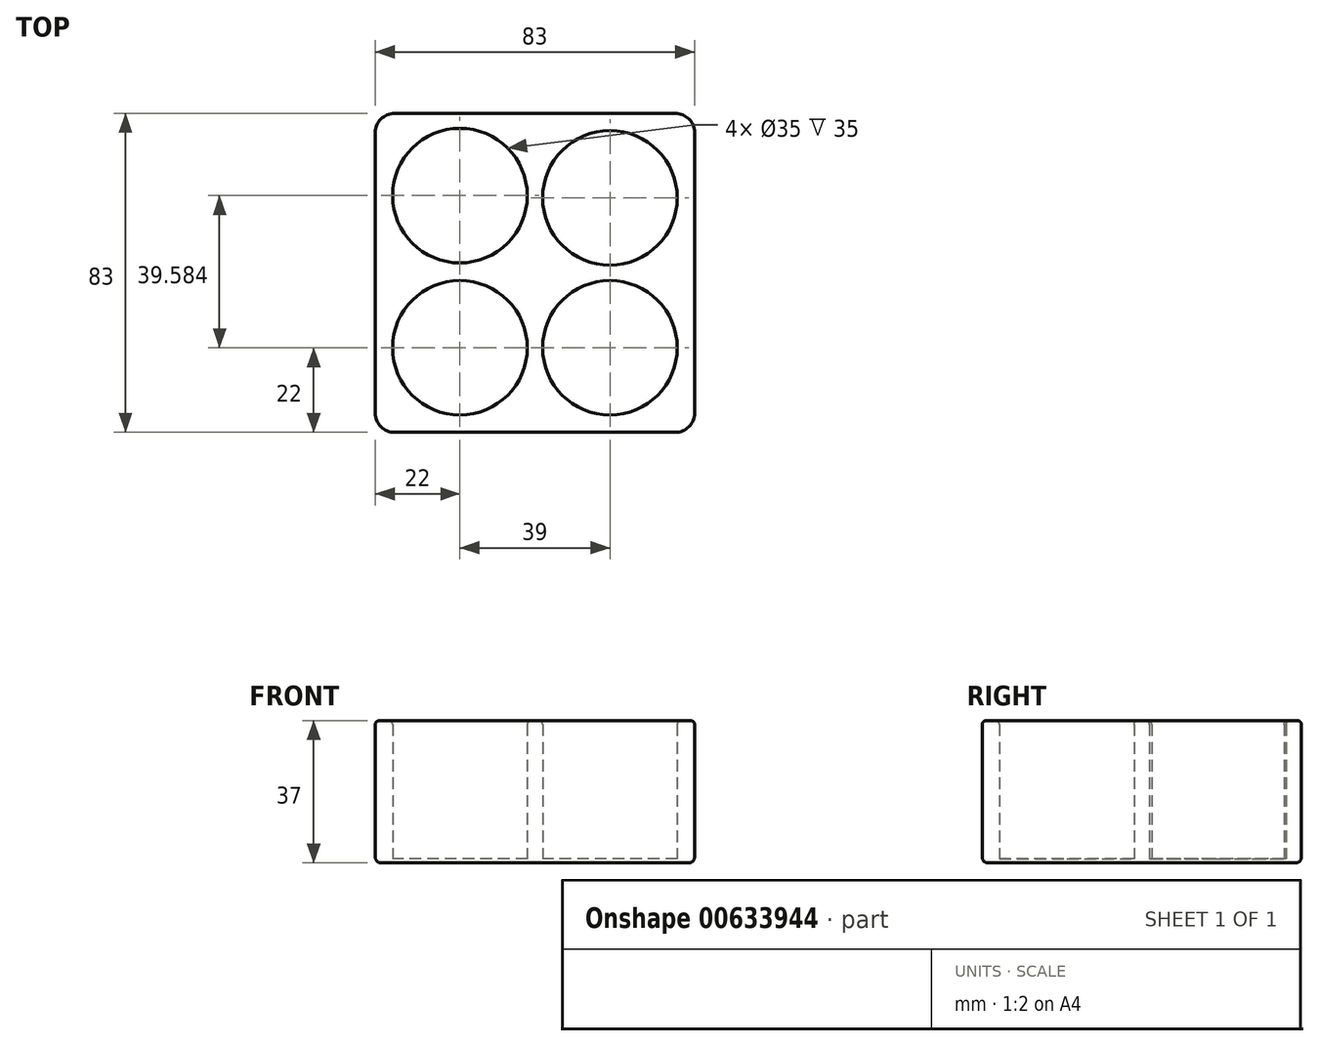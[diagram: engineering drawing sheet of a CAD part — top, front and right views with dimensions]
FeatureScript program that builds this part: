
annotation { "Feature Type Name" : "Feature", "Feature Type Description" : "" }
export const myFeature = defineFeature(function(context is Context, id is Id, definition is map)
    precondition{}
    {
        {
            var Q0;
            Q0=qCreatedBy(makeId("Top.planeOp"),FACE);
            var sketch = newSketch(context, id + "F0", { "sketchPlane" : qUnion([Q0])});
            skPoint(sketch, "E0.middle", {"position": v(0, 0) * mm});
            skCircle(sketch, "E1", {"center": v(-22.5, 0) * mm, "radius": 17.5 * mm});
            skCircle(sketch, "E2", {"center": v(16.5, 0) * mm, "radius": 17.5 * mm});
            skCircle(sketch, "E3", {"center": v(-22.5, 39.58) * mm, "radius": 17.5 * mm});
            skCircle(sketch, "E4", {"center": v(16.5, 39) * mm, "radius": 17.5 * mm});
            skPoint(sketch, "E0.top.end.orphan", {"position": v(47.5, -50) * mm});
            skPoint(sketch, "E0.left.end.orphan", {"position": v(-47.5, -50) * mm});
            skPoint(sketch, "E5.orphan", {"position": v(47.5, 50) * mm});
            skPoint(sketch, "E6.orphan", {"position": v(-47.5, 50) * mm});
            skLineSegment(sketch, "E7.bottom", {"start": v(-44.5, 61) * mm, "end": v(38.5, 61) * mm});
            skLineSegment(sketch, "E7.top", {"start": v(-44.5, -22) * mm, "end": v(38.5, -22) * mm});
            skLineSegment(sketch, "E7.left", {"start": v(-44.5, 61) * mm, "end": v(-44.5, -22) * mm});
            skLineSegment(sketch, "E7.right", {"start": v(38.5, 61) * mm, "end": v(38.5, -22) * mm});
            skSolve(sketch);
        }
        {
            var Q0;
            Q0=qSketchRegion(id+"F0",true);
            var Q1;
            Q1=makeQuery(id+"F0.imprint","IMPRINT",FACE,{"disambiguationData":[TD([[makeQuery(id+"F0.imprint","IMPRINT",EDGE,{"derivedFrom":sQuery(id+"F0.wireOp",EDGE,"E0.bottom")}),-1.0]])]});
            extrude(context, id + "F1", {"entities" : qUnion([Q0, Q1]), "depth" : 36 * mm, "offsetDistance" : 25 * mm});
        }
        {
            var Q0;
            Q0=makeQuery(id+"F1.opExtrude","CAP_FACE",FACE,{"disambiguationData":[OSD([sQuery(id+"F0.wireOp",EDGE,"E1"),sQuery(id+"F0.wireOp",EDGE,"E2"),sQuery(id+"F0.wireOp",EDGE,"E3"),sQuery(id+"F0.wireOp",EDGE,"E4"),sQuery(id+"F0.wireOp",EDGE,"E7.bottom"),sQuery(id+"F0.wireOp",EDGE,"E7.top"),sQuery(id+"F0.wireOp",EDGE,"E7.left"),sQuery(id+"F0.wireOp",EDGE,"E7.right")])],"isStart":false});
            fillet(context, id + "F2", {"entities" : qUnion([Q0]), "radius" : 1 * mm, "tangentPropagation" : true, "allowEdgeOverflow" : false});
        }
        {
            var Q0;
            Q0=makeQuery(id+"F1.opExtrude","CAP_FACE",FACE,{"disambiguationData":[OSD([sQuery(id+"F0.wireOp",EDGE,"E1"),sQuery(id+"F0.wireOp",EDGE,"E2"),sQuery(id+"F0.wireOp",EDGE,"E3"),sQuery(id+"F0.wireOp",EDGE,"E4"),sQuery(id+"F0.wireOp",EDGE,"E7.bottom"),sQuery(id+"F0.wireOp",EDGE,"E7.top"),sQuery(id+"F0.wireOp",EDGE,"E7.left"),sQuery(id+"F0.wireOp",EDGE,"E7.right")])],"isStart":true});
            var sketch = newSketch(context, id + "F3", { "sketchPlane" : qUnion([Q0])});
            skLineSegment(sketch, "E8.bottom", {"start": v(-44.5, 22) * mm, "end": v(38.5, 22) * mm});
            skLineSegment(sketch, "E8.top", {"start": v(-44.5, -61) * mm, "end": v(38.5, -61) * mm});
            skLineSegment(sketch, "E8.left", {"start": v(-44.5, 22) * mm, "end": v(-44.5, -61) * mm});
            skLineSegment(sketch, "E8.right", {"start": v(38.5, 22) * mm, "end": v(38.5, -61) * mm});
            skSolve(sketch);
        }
        {
            var Q0;
            Q0 = qSketchRegion(id + "F3", true);
            extrude(context, id + "F4", {"entities" : qUnion([Q0]), "operationType" : NewBodyOperationType.ADD, "depth" : 1 * mm, "offsetDistance" : 25 * mm});
        }
        {
            var Q0;
            Q0=makeQuery(id+"F4.boolean.opBoolean","MERGE",EDGE,{"derivedFrom":[makeQuery(id+"F1.opExtrude","SWEPT_EDGE",EDGE,{"disambiguationData":[OSD([sQuery(id+"F0.wireOp",EDGE,"E7.bottom"),sQuery(id+"F0.wireOp",EDGE,"E7.left")])]}),makeQuery(id+"F4.opExtrude","SWEPT_EDGE",EDGE,{"disambiguationData":[OSD([sQuery(id+"F3.wireOp",EDGE,"E8.top"),sQuery(id+"F3.wireOp",EDGE,"E8.left")])]})]});
            var Q1;
            Q1=makeQuery(id+"F4.boolean.opBoolean","MERGE",EDGE,{"derivedFrom":[makeQuery(id+"F1.opExtrude","SWEPT_EDGE",EDGE,{"disambiguationData":[OSD([sQuery(id+"F0.wireOp",EDGE,"E7.top"),sQuery(id+"F0.wireOp",EDGE,"E7.left")])]}),makeQuery(id+"F4.opExtrude","SWEPT_EDGE",EDGE,{"disambiguationData":[OSD([sQuery(id+"F3.wireOp",EDGE,"E8.bottom"),sQuery(id+"F3.wireOp",EDGE,"E8.left")])]})]});
            var Q2;
            Q2=makeQuery(id+"F4.boolean.opBoolean","MERGE",EDGE,{"derivedFrom":[makeQuery(id+"F1.opExtrude","SWEPT_EDGE",EDGE,{"disambiguationData":[OSD([sQuery(id+"F0.wireOp",EDGE,"E7.top"),sQuery(id+"F0.wireOp",EDGE,"E7.right")])]}),makeQuery(id+"F4.opExtrude","SWEPT_EDGE",EDGE,{"disambiguationData":[OSD([sQuery(id+"F3.wireOp",EDGE,"E8.bottom"),sQuery(id+"F3.wireOp",EDGE,"E8.right")])]})]});
            var Q3;
            Q3=makeQuery(id+"F4.boolean.opBoolean","MERGE",EDGE,{"derivedFrom":[makeQuery(id+"F1.opExtrude","SWEPT_EDGE",EDGE,{"disambiguationData":[OSD([sQuery(id+"F0.wireOp",EDGE,"E7.bottom"),sQuery(id+"F0.wireOp",EDGE,"E7.right")])]}),makeQuery(id+"F4.opExtrude","SWEPT_EDGE",EDGE,{"disambiguationData":[OSD([sQuery(id+"F3.wireOp",EDGE,"E8.top"),sQuery(id+"F3.wireOp",EDGE,"E8.right")])]})]});
            fillet(context, id + "F5", {"entities" : qUnion([Q0, Q1, Q2, Q3]), "radius" : 5 * mm, "tangentPropagation" : true, "allowEdgeOverflow" : false});
        }
        {
            var Q0;
            Q0=makeQuery(id+"F4.opExtrude","CAP_FACE",FACE,{"disambiguationData":[OSD([sQuery(id+"F3.wireOp",EDGE,"E8.bottom"),sQuery(id+"F3.wireOp",EDGE,"E8.top"),sQuery(id+"F3.wireOp",EDGE,"E8.left"),sQuery(id+"F3.wireOp",EDGE,"E8.right")])],"isStart":false});
            fillet(context, id + "F6", {"entities" : qUnion([Q0]), "radius" : 1.5 * mm, "tangentPropagation" : true, "allowEdgeOverflow" : false});
        }
    });
